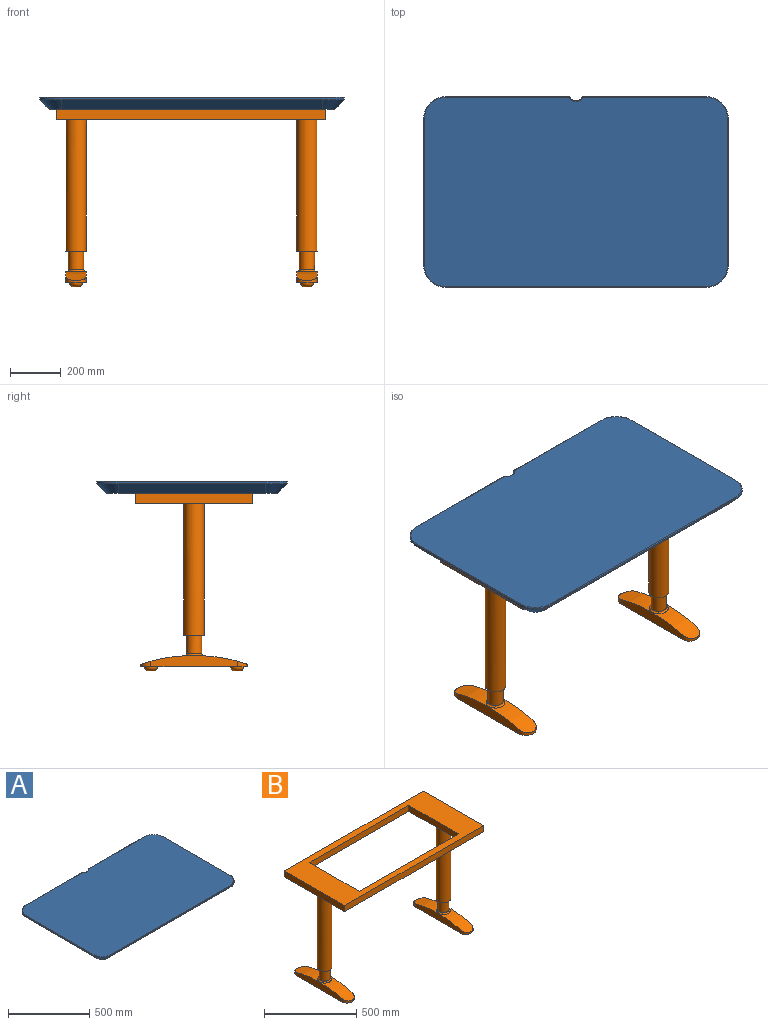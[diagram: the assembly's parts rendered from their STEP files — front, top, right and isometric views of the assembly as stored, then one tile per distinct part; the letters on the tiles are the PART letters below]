
ASSEMBLY  parts=2 mates=1
PART A: 58 faces, bbox 1214x764x47 mm
  f0: plane 486.67x7mm, normal (0,1,0), area 3406.7mm2, adj f8,f12,f26,f31
  f1: plane 580x7mm, normal (-1,0,0), area 4060mm2, adj f8,f9,f15,f32
  f2: plane 1030x7mm, normal (0,-1,0), area 7210mm2, adj f9,f10,f19,f28
  f3: plane 580x7mm, normal (1,0,0), area 4060mm2, adj f10,f11,f16,f23
  f4: plane 486.67x7mm, normal (0,1,0), area 3406.7mm2, adj f11,f12,f21,f22
  f5: cylinder r=31.25mm len=51.69mm, axis (0,0,-1), area 1052.4mm2, adj f12,f21,f26,f27
  f6: plane 1194x744mm, normal (0,0,1), area 881966.9mm2, adj f20,f22,f23,f25,f27,f28,f30,f31
  f7: plane 1126x676mm, normal (0,0,-1), area 758293.1mm2, adj f12,f13,f14,f15,f16,f17,f18,f19
  f8: cylinder r=85mm len=85mm, axis (0,0,1), area 934.6mm2, adj f0,f1,f13,f33
  f9: cylinder r=85mm len=85mm, axis (0,0,-1), area 934.6mm2, adj f1,f2,f17,f30
  f10: cylinder r=85mm len=85mm, axis (0,0,1), area 934.6mm2, adj f2,f3,f18,f25
  f11: cylinder r=85mm len=85mm, axis (0,0,-1), area 934.6mm2, adj f3,f4,f14,f20
  f12: plane 1030x37mm, normal (0,0.71,-0.71), area 53093.8mm2, adj f0,f4,f5,f7,f13,f14,f21,f26
  f13: cone r=48mm half-angle=45deg, axis (0,0,1), area 5465.9mm2, adj f7,f8,f12,f15
  f14: cone r=48mm half-angle=45deg, axis (0,0,1), area 5465.9mm2, adj f7,f11,f12,f16
  f15: plane 580x37mm, normal (-0.71,0,-0.71), area 30349mm2, adj f1,f7,f13,f17
  f16: plane 580x37mm, normal (0.71,0,-0.71), area 30349mm2, adj f3,f7,f14,f18
  f17: cone r=48mm half-angle=45deg, axis (0,0,1), area 5465.9mm2, adj f7,f9,f15,f19
  f18: cone r=48mm half-angle=45deg, axis (0,0,1), area 5465.9mm2, adj f7,f10,f16,f19
  f19: plane 1030x37mm, normal (0,-0.71,-0.71), area 53895.7mm2, adj f2,f7,f17,f18
  f20: torus R=82mm, axis (0,0,1), area 621.1mm2, adj f6,f11,f22,f23
  f21: cylinder r=3mm len=8.31mm, axis (0,0,-1), area 21.8mm2, adj f4,f5,f12,f24
  f22: cylinder r=3mm len=486.67mm, axis (1,0,0), area 2293.4mm2, adj f4,f6,f20,f24
  f23: cylinder r=3mm len=580mm, axis (0,-1,0), area 2733.2mm2, adj f3,f6,f20,f25
  f24: sphere r=3mm, area 8.8mm2, adj f21,f22,f27
  f25: torus R=82mm, axis (0,0,1), area 621.1mm2, adj f6,f10,f23,f28
  f26: cylinder r=3mm len=8.31mm, axis (0,0,-1), area 21.8mm2, adj f0,f5,f12,f29
  f27: torus R=34.25mm, axis (0,0,1), area 296.9mm2, adj f5,f6,f24,f29
  f28: cylinder r=3mm len=1030mm, axis (-1,0,0), area 4853.8mm2, adj f2,f6,f25,f30
  f29: sphere r=3mm, area 8.8mm2, adj f26,f27,f31
  f30: torus R=82mm, axis (0,0,1), area 621.1mm2, adj f6,f9,f28,f32
  f31: cylinder r=3mm len=486.67mm, axis (1,0,0), area 2293.4mm2, adj f0,f6,f29,f33
  f32: cylinder r=3mm len=580mm, axis (0,1,0), area 2733.2mm2, adj f1,f6,f30,f33
  f33: torus R=82mm, axis (0,0,1), area 621.1mm2, adj f6,f8,f31,f32
  f34: cone r=0mm half-angle=59deg, axis (0,0,-1), area 88mm2, adj f35
  f35: cylinder r=4.9mm len=12.5mm, axis (0,0,-1), area 384.8mm2, adj f7,f34
  f36: cone r=0mm half-angle=59deg, axis (0,0,-1), area 88mm2, adj f37
  f37: cylinder r=4.9mm len=12.5mm, axis (0,0,-1), area 384.8mm2, adj f7,f36
  f38: cone r=0mm half-angle=59deg, axis (0,0,-1), area 88mm2, adj f39
  f39: cylinder r=4.9mm len=12.5mm, axis (0,0,-1), area 384.8mm2, adj f7,f38
  f40: cone r=0mm half-angle=59deg, axis (0,0,-1), area 88mm2, adj f41
  f41: cylinder r=4.9mm len=12.5mm, axis (0,0,-1), area 384.8mm2, adj f7,f40
  f42: cone r=0mm half-angle=59deg, axis (0,0,-1), area 88mm2, adj f43
  f43: cylinder r=4.9mm len=12.5mm, axis (0,0,-1), area 384.8mm2, adj f7,f42
  f44: cone r=0mm half-angle=59deg, axis (0,0,-1), area 88mm2, adj f45
  f45: cylinder r=4.9mm len=12.5mm, axis (0,0,-1), area 384.8mm2, adj f7,f44
  f46: cone r=0mm half-angle=59deg, axis (0,0,-1), area 88mm2, adj f47
  f47: cylinder r=4.9mm len=12.5mm, axis (0,0,-1), area 384.8mm2, adj f7,f46
  f48: cone r=0mm half-angle=59deg, axis (0,0,-1), area 88mm2, adj f49
  f49: cylinder r=4.9mm len=12.5mm, axis (0,0,-1), area 384.8mm2, adj f7,f48
  f50: cone r=0mm half-angle=59deg, axis (0,0,-1), area 88mm2, adj f51
  f51: cylinder r=4.9mm len=12.5mm, axis (0,0,-1), area 384.8mm2, adj f7,f50
  f52: cone r=0mm half-angle=59deg, axis (0,0,-1), area 88mm2, adj f53
  f53: cylinder r=4.9mm len=12.5mm, axis (0,0,-1), area 384.8mm2, adj f7,f52
  f54: cone r=0mm half-angle=59deg, axis (0,0,-1), area 88mm2, adj f55
  f55: cylinder r=4.9mm len=12.5mm, axis (0,0,-1), area 384.8mm2, adj f7,f54
  f56: cone r=0mm half-angle=59deg, axis (0,0,-1), area 88mm2, adj f57
  f57: cylinder r=4.9mm len=12.5mm, axis (0,0,-1), area 384.8mm2, adj f7,f56
PART B: 48 faces, bbox 1060x460x700 mm
  f0: plane 340x45mm, normal (1,0,0), area 12962mm2, adj f1,f2,f37,f38,f41,f43
  f1: plane 37.77x8.18mm, normal (0,0,1), area 176.6mm2, adj f0,f39,f41,f43
  f2: cylinder r=40mm len=80mm, axis (0,0,1), area 1870.3mm2, adj f0,f36,f37,f43
  f3: plane 37.77x8.18mm, normal (0,0,1), area 176.6mm2, adj f36,f39,f41,f43
  f4: plane 340x45mm, normal (1,0,0), area 12962mm2, adj f7,f8,f22,f23,f25,f27
  f5: plane 340x45mm, normal (-1,0,0), area 12962mm2, adj f6,f8,f22,f23,f25,f27
  f6: plane 37.77x8.18mm, normal (0,0,1), area 176.6mm2, adj f5,f24,f25,f27
  f7: plane 37.77x8.18mm, normal (0,0,1), area 176.6mm2, adj f4,f24,f25,f27
  f8: cylinder r=40mm len=80mm, axis (0,0,1), area 1870.3mm2, adj f4,f5,f22,f25
  f9: plane 760x40mm, normal (0,1,0), area 30400mm2, adj f10,f16,f17,f18
  f10: plane 380x40mm, normal (-1,0,0), area 15200mm2, adj f9,f11,f17,f18
  f11: plane 760x40mm, normal (0,-1,0), area 30400mm2, adj f10,f16,f17,f18
  f12: plane 460x40mm, normal (1,0,0), area 18400mm2, adj f13,f15,f17,f18
  f13: plane 1060x40mm, normal (0,-1,0), area 42400mm2, adj f12,f14,f17,f18
  f14: plane 460x40mm, normal (-1,0,0), area 18400mm2, adj f13,f15,f17,f18
  f15: plane 1060x40mm, normal (0,1,0), area 42400mm2, adj f12,f14,f17,f18
  f16: plane 380x40mm, normal (1,0,0), area 15200mm2, adj f9,f11,f17,f18
  f17: plane 1060x460mm, normal (0,0,-1), area 188746.9mm2, adj f9,f10,f11,f12,f13,f14,f15,f16
  f18: plane 1060x460mm, normal (0,0,1), area 198800mm2, adj f9,f10,f11,f12,f13,f14,f15,f16
  f19: cylinder r=40mm len=520mm, axis (0,0,1), area 130690.3mm2, adj f17,f20
  f20: plane 80x80mm, normal (0,0,-1), area 2199.1mm2, adj f19,f21
  f21: cylinder r=30mm len=73mm, axis (0,0,1), area 13760.2mm2, adj f20,f24
  f22: plane 420x80mm, normal (0,0,-1), area 28299.6mm2, adj f4,f5,f8,f23,f31,f32
  f23: cylinder r=40mm len=80mm, axis (0,0,1), area 1870.1mm2, adj f4,f5,f22,f27
  f24: torus R=37mm, axis (0,0,-1), area 2248.4mm2, adj f6,f7,f21,f26,f28
  f25: cylinder r=590.91mm len=191.12mm, axis (1,0,0), area 14889.4mm2, adj f4,f5,f6,f7,f8,f26
  f26: plane 63.63x18.11mm, normal (0,0,-1), area 816.1mm2, adj f24,f25
  f27: cylinder r=590.91mm len=191.12mm, axis (1,0,0), area 14888.2mm2, adj f4,f5,f6,f7,f23,f28
  f28: plane 63.63x18.11mm, normal (0,0,-1), area 816.1mm2, adj f24,f27
  f29: plane 20x20mm, normal (0,0,-1), area 314.2mm2, adj f32
  f30: plane 20x20mm, normal (0,0,-1), area 314.2mm2, adj f31
  f31: torus R=10mm, axis (0,0,-1), area 2894.2mm2, adj f22,f30
  f32: torus R=10mm, axis (0,0,-1), area 2894.2mm2, adj f22,f29
  f33: cylinder r=40mm len=520mm, axis (0,0,1), area 130690.3mm2, adj f17,f34
  f34: plane 80x80mm, normal (0,0,-1), area 2199.1mm2, adj f33,f35
  f35: cylinder r=30mm len=73mm, axis (0,0,1), area 13760.2mm2, adj f34,f39
  f36: plane 340x45mm, normal (-1,0,0), area 12962mm2, adj f2,f3,f37,f38,f41,f43
  f37: plane 420x80mm, normal (0,0,-1), area 28299.6mm2, adj f0,f2,f36,f38,f46,f47
  f38: cylinder r=40mm len=80mm, axis (0,0,1), area 1870.1mm2, adj f0,f36,f37,f41
  f39: torus R=37mm, axis (0,0,-1), area 2248.4mm2, adj f1,f3,f35,f40,f42
  f40: plane 63.63x18.11mm, normal (0,0,-1), area 816.1mm2, adj f39,f41
  f41: cylinder r=590.91mm len=191.12mm, axis (-1,0,0), area 14888.2mm2, adj f0,f1,f3,f36,f38,f40
  f42: plane 63.63x18.11mm, normal (0,0,-1), area 816.1mm2, adj f39,f43
  f43: cylinder r=590.91mm len=191.12mm, axis (-1,0,0), area 14889.4mm2, adj f0,f1,f2,f3,f36,f42
  f44: plane 20x20mm, normal (0,0,-1), area 314.2mm2, adj f47
  f45: plane 20x20mm, normal (0,0,-1), area 314.2mm2, adj f46
  f46: torus R=10mm, axis (0,0,-1), area 2894.2mm2, adj f37,f45
  f47: torus R=10mm, axis (0,0,-1), area 2894.2mm2, adj f37,f44
PLACE A t=(126.97,170.97,-265.78)mm
PLACE B t=(124.95,162.68,-265.78)mm
MATE planar B.f18 <-> A.f7  axis (0,0,1) through (124.95,162.68,-265.78)mm
